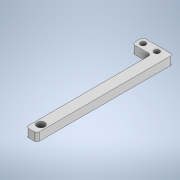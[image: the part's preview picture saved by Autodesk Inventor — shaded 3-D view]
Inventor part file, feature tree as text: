
AUTODESK INVENTOR PART (.ipt)
format: ipt  version: 2020 (Build 240168000, 168)  size: 140,288 bytes
history: native  units: mm
features: extrude x2, sketch x1, fillet x1
ambient origin geometry x8: Origin, YZ Plane, XZ Plane, XY Plane, X Axis, Y Axis, Z Axis, Center Point
bodies: Solide1 (feature_tree)
feature tree (4):
  sketch  "Esquisse1"
  extrude  "Extrusion1"  Depth=8.0mm
  fillet  "Congé1"  Radius=100.0mm
  extrude  "Extrusion2"  Depth=8.0mm
